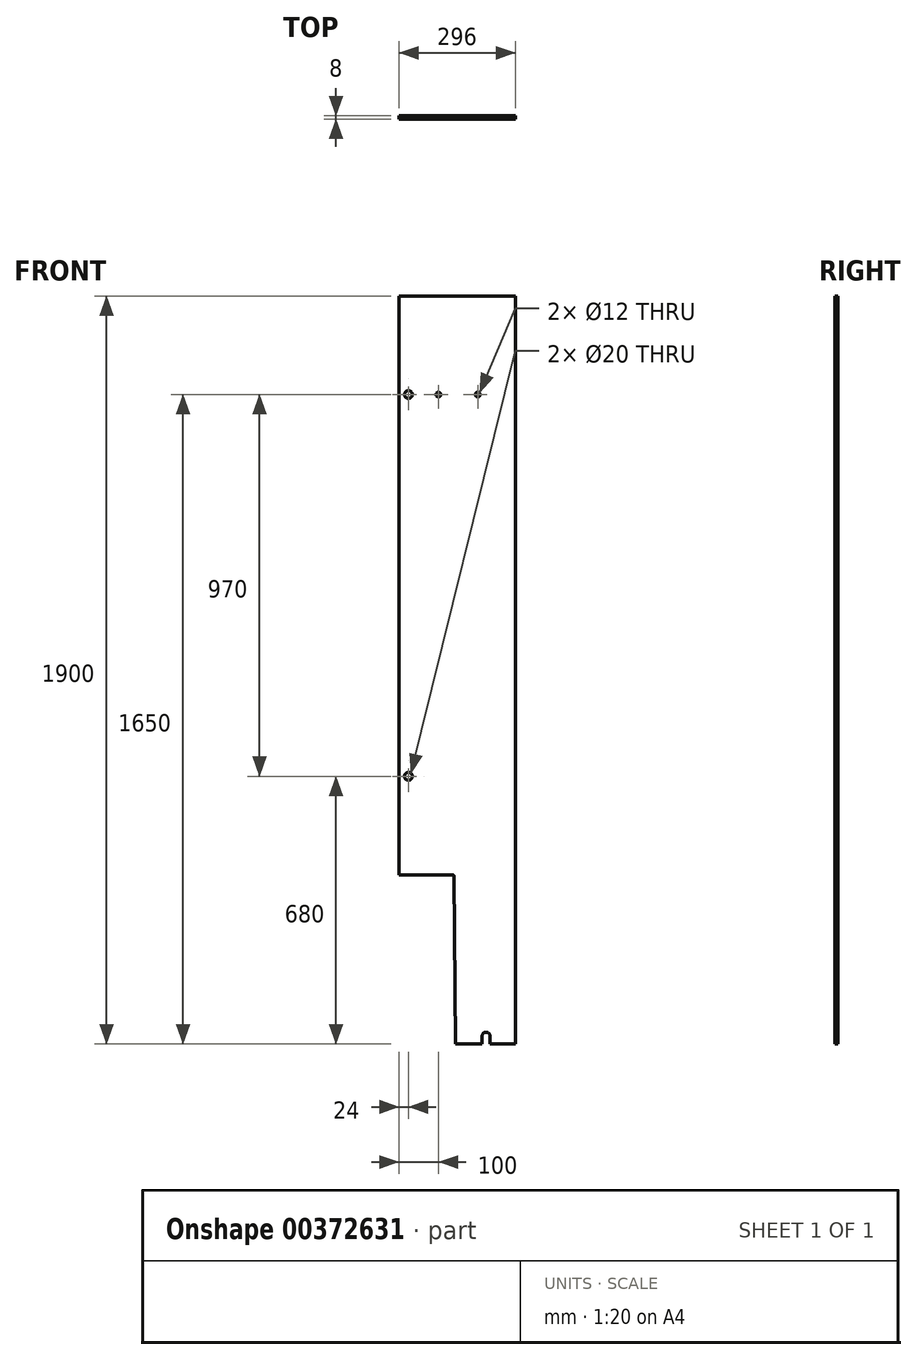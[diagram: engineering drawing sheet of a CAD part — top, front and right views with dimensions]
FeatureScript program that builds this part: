
annotation { "Feature Type Name" : "Feature", "Feature Type Description" : "" }
export const myFeature = defineFeature(function(context is Context, id is Id, definition is map)
    precondition{}
    {
        {
            var Q0;
            Q0=qCreatedBy(makeId("Front.planeOp"),FACE);
            var sketch = newSketch(context, id + "F0", { "sketchPlane" : qUnion([Q0])});
            skLineSegment(sketch, "E0.bottom", {"start": v(-148, 950) * mm, "end": v(148, 950) * mm});
            skLineSegment(sketch, "E0.top", {"start": v(-148, -950) * mm, "end": v(63, -950) * mm, "construction": true});
            skLineSegment(sketch, "E0.left", {"start": v(-148, 950) * mm, "end": v(-148, -950) * mm, "construction": true});
            skLineSegment(sketch, "E0.right", {"start": v(148, 950) * mm, "end": v(148, -950) * mm});
            skPoint(sketch, "E0.middle", {"position": v(0, 0) * mm});
            skCircle(sketch, "E1", {"center": v(-124, 700) * mm, "radius": 10 * mm});
            skCircle(sketch, "E2", {"center": v(-124, -270) * mm, "radius": 10 * mm});
            skCircle(sketch, "E3", {"center": v(52, 700) * mm, "radius": 6 * mm});
            skCircle(sketch, "E4", {"center": v(-48, 700) * mm, "radius": 6 * mm});
            skArc(sketch, "E5", {"start": v(83, -930) * mm, "mid": v(73, -920) * mm, "end": v(63, -930) * mm});
            skLineSegment(sketch, "E6", {"start": v(-124, 700) * mm, "end": v(-124, -270) * mm, "construction": true});
            skLineSegment(sketch, "E7", {"start": v(-48, 700) * mm, "end": v(52, 700) * mm, "construction": true});
            skLineSegment(sketch, "E8", {"start": v(52, 700) * mm, "end": v(128, 700) * mm, "construction": true});
            skLineSegment(sketch, "E9", {"start": v(128, 700) * mm, "end": v(128, -270) * mm, "construction": true});
            skLineSegment(sketch, "E10", {"start": v(-148, 950) * mm, "end": v(-148, -520) * mm});
            skLineSegment(sketch, "E11", {"start": v(-148, -520) * mm, "end": v(-12.95, -520) * mm});
            skLineSegment(sketch, "E12", {"start": v(-7.95, -524.95) * mm, "end": v(-4, -950) * mm});
            skLineSegment(sketch, "E13", {"start": v(-4, -950) * mm, "end": v(63, -950) * mm});
            skLineSegment(sketch, "E14", {"start": v(-124, -270) * mm, "end": v(128, -270) * mm, "construction": true});
            skLineSegment(sketch, "E15", {"start": v(83, -930) * mm, "end": v(83, -950) * mm});
            skLineSegment(sketch, "E16", {"start": v(63, -930) * mm, "end": v(63, -950) * mm});
            skLineSegment(sketch, "E17.trimOffspring", {"start": v(83, -950) * mm, "end": v(148, -950) * mm, "construction": true});
            skLineSegment(sketch, "E18.trimOffspring", {"start": v(83, -950) * mm, "end": v(148, -950) * mm});
            skLineSegment(sketch, "E19", {"start": v(-124, 700) * mm, "end": v(-48, 700) * mm, "construction": true});
            skPoint(sketch, "E20.visualSharp", {"position": v(-8, -520) * mm});
            skArc(sketch, "E20.filletArc", {"start": v(-7.95, -524.95) * mm, "mid": v(-9.43, -521.45) * mm, "end": v(-12.95, -520) * mm});
            skSolve(sketch);
        }
        {
            var Q0;
            Q0=qSketchRegion(id+"F0",true);
            extrude(context, id + "F1", {"entities" : qUnion([Q0]), "depth" : 8 * mm});
        }
    });
